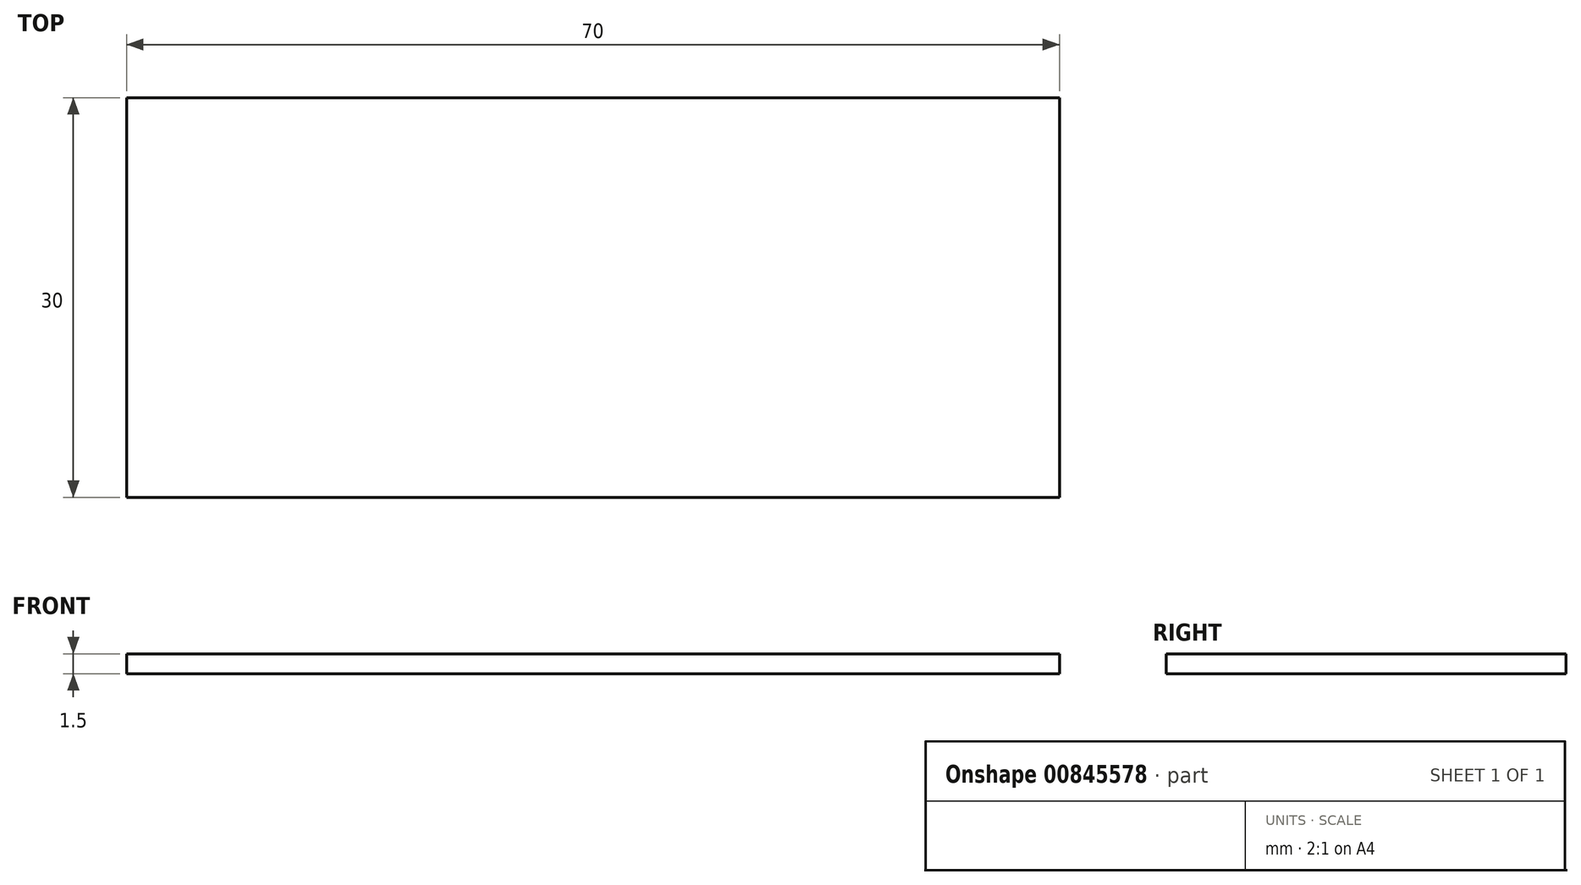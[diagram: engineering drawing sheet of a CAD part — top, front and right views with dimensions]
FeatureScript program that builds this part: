
annotation { "Feature Type Name" : "Feature", "Feature Type Description" : "" }
export const myFeature = defineFeature(function(context is Context, id is Id, definition is map)
    precondition{}
    {
        {
            var Q0;
            Q0=qCreatedBy(makeId("Top.planeOp"),FACE);
            var sketch = newSketch(context, id + "F0", { "sketchPlane" : qUnion([Q0])});
            skLineSegment(sketch, "E0.bottom", {"start": v(-35, -15) * mm, "end": v(35, -15) * mm});
            skLineSegment(sketch, "E0.top", {"start": v(-35, 15) * mm, "end": v(35, 15) * mm});
            skLineSegment(sketch, "E0.left", {"start": v(-35, -15) * mm, "end": v(-35, 15) * mm});
            skLineSegment(sketch, "E0.right", {"start": v(35, -15) * mm, "end": v(35, 15) * mm});
            skPoint(sketch, "E0.middle", {"position": v(0, 0) * mm});
            skSolve(sketch);
        }
        {
            var Q0;
            Q0=makeQuery(id+"F0.imprint","IMPRINT",FACE,{"disambiguationData":[TD([[makeQuery(id+"F0.imprint","IMPRINT",EDGE,{"derivedFrom":sQuery(id+"F0.wireOp",EDGE,"E0.bottom")}),1.0]])]});
            extrude(context, id + "F1", {"entities" : qUnion([Q0]), "depth" : 1.5 * mm, "offsetDistance" : 25 * mm});
        }
    });
